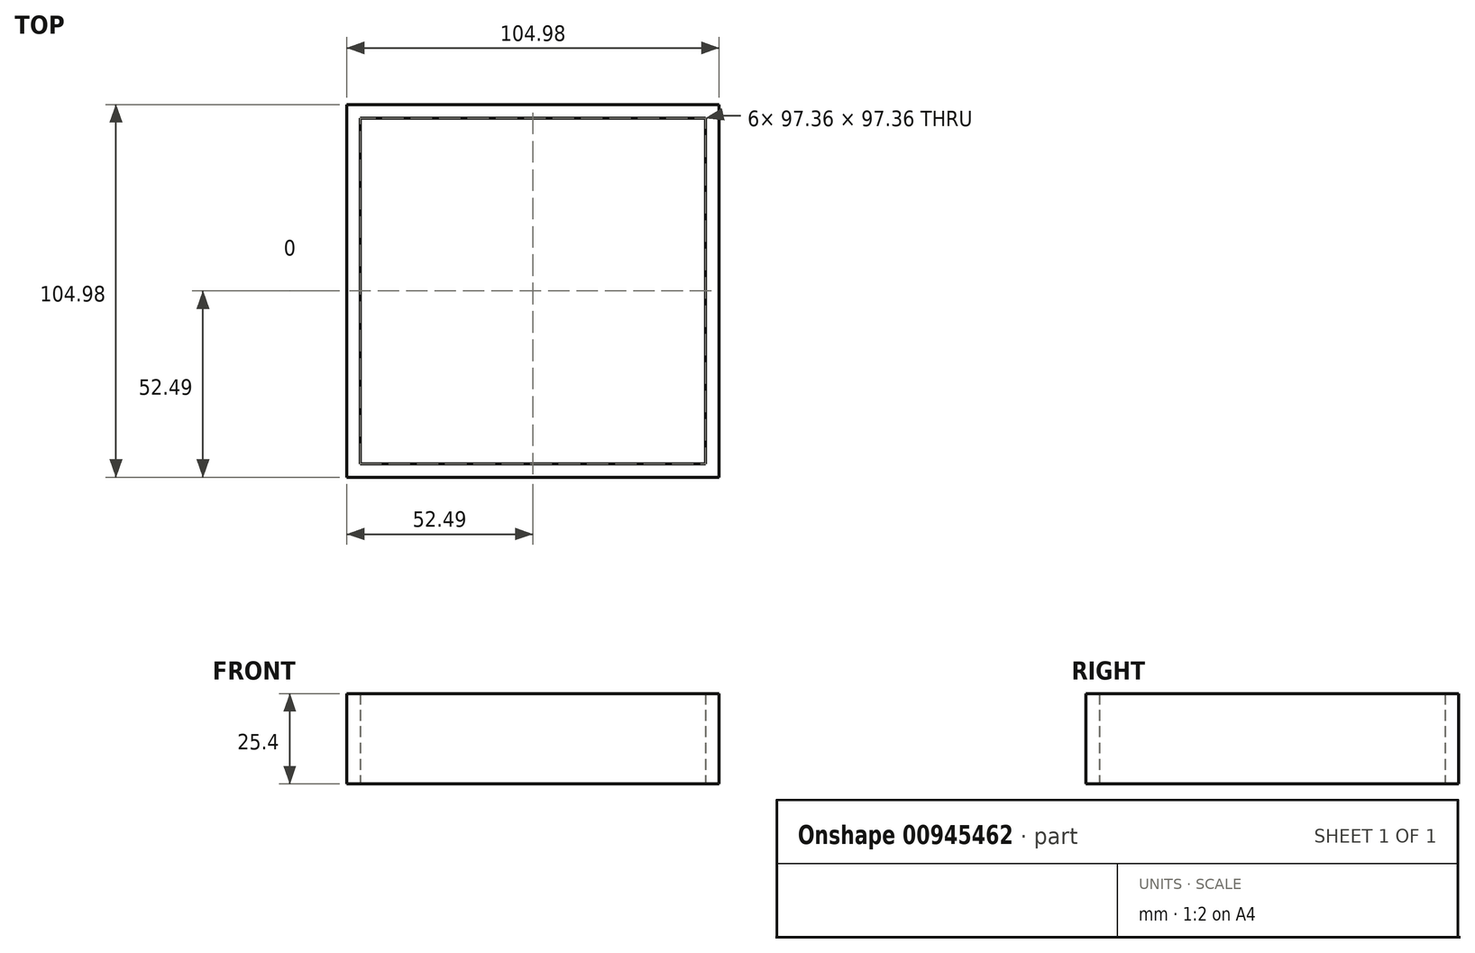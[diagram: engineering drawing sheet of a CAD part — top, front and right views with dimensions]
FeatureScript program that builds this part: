
annotation { "Feature Type Name" : "Feature", "Feature Type Description" : "" }
export const myFeature = defineFeature(function(context is Context, id is Id, definition is map)
    precondition{}
    {
        {
            var Q0;
            Q0=qCreatedBy(makeId("Top.planeOp"),FACE);
            var sketch = newSketch(context, id + "F0", { "sketchPlane" : qUnion([Q0])});
            skLineSegment(sketch, "E0.bottom", {"start": v(48.68, 48.68) * mm, "end": v(-48.68, 48.68) * mm});
            skLineSegment(sketch, "E0.top", {"start": v(48.68, -48.68) * mm, "end": v(-48.68, -48.68) * mm});
            skLineSegment(sketch, "E0.left", {"start": v(48.68, 48.68) * mm, "end": v(48.68, -48.68) * mm});
            skLineSegment(sketch, "E0.right", {"start": v(-48.68, 48.68) * mm, "end": v(-48.68, -48.68) * mm});
            skPoint(sketch, "E0.middle", {"position": v(0, 0) * mm});
            skSolve(sketch);
        }
        {
            var Q0;
            Q0=qCreatedBy(makeId("Top.planeOp"),FACE);
            var sketch = newSketch(context, id + "F1", { "sketchPlane" : qUnion([Q0])});
            skLineSegment(sketch, "E1.bottom", {"start": v(52.49, 52.49) * mm, "end": v(-52.49, 52.49) * mm});
            skLineSegment(sketch, "E1.top", {"start": v(52.49, -52.49) * mm, "end": v(-52.49, -52.49) * mm});
            skLineSegment(sketch, "E1.left", {"start": v(52.49, 52.49) * mm, "end": v(52.49, -52.49) * mm});
            skLineSegment(sketch, "E1.right", {"start": v(-52.49, 52.49) * mm, "end": v(-52.49, -52.49) * mm});
            skPoint(sketch, "E1.middle", {"position": v(0, 0) * mm});
            skSolve(sketch);
        }
        {
            var Q0;
            Q0=qSketchRegion(id+"F1",true);
            extrude(context, id + "F2", {"entities" : qUnion([Q0]), "depth" : 25.4 * mm, "offsetDistance" : 25.4 * mm});
        }
        {
            var Q0;
            Q0=qSketchRegion(id+"F0",true);
            extrude(context, id + "F3", {"entities" : qUnion([Q0]), "operationType" : NewBodyOperationType.REMOVE, "depth" : 25.4 * mm, "offsetDistance" : 25.4 * mm});
        }
    });
